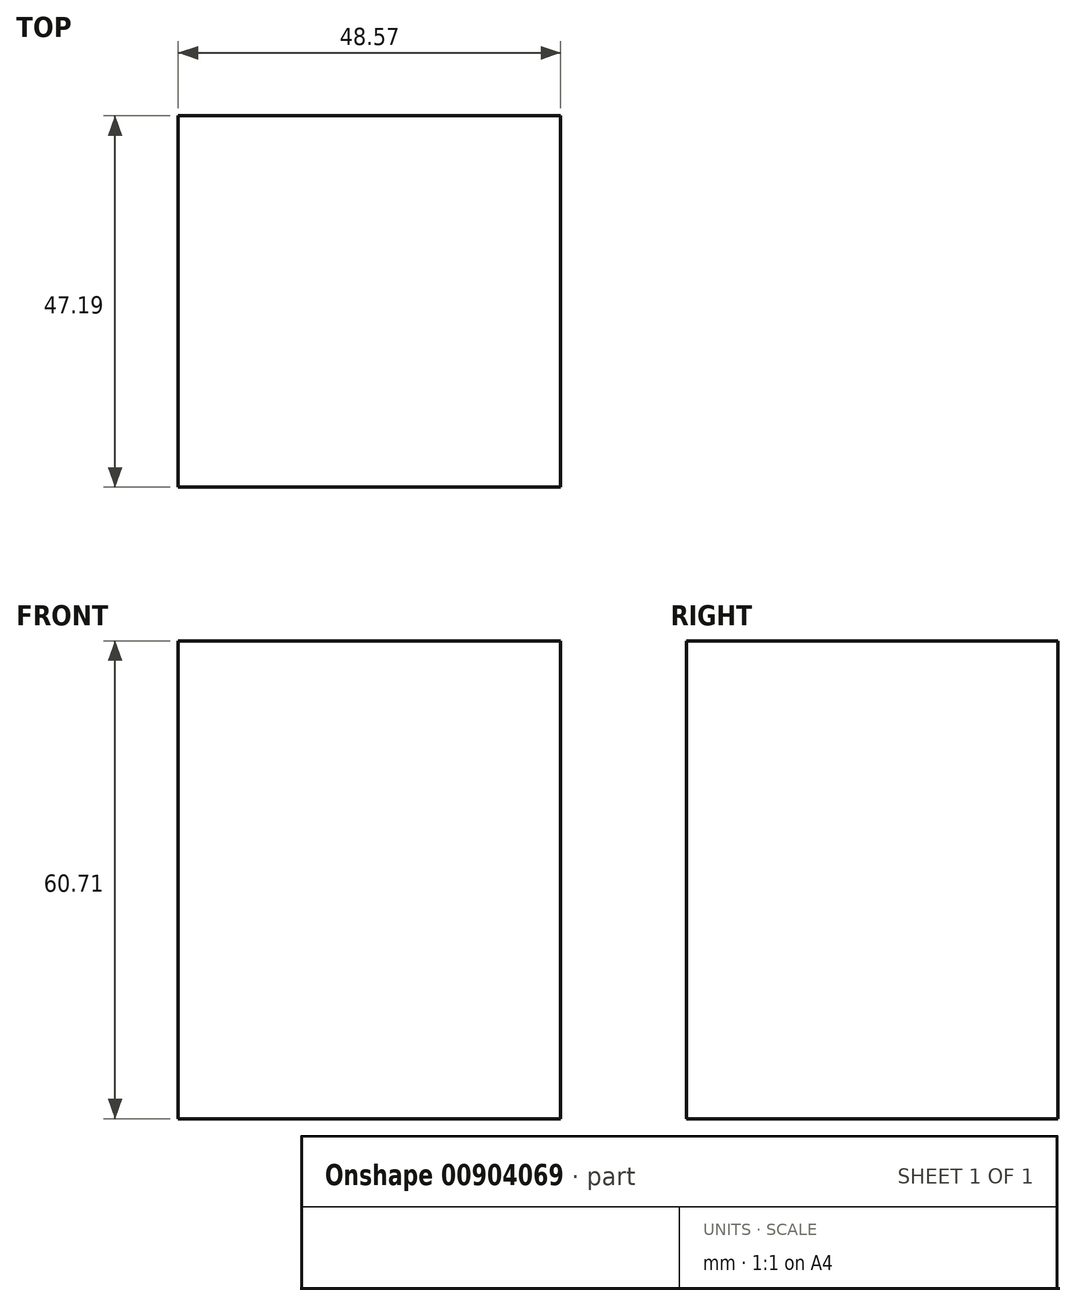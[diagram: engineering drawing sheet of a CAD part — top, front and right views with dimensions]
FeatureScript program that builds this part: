
annotation { "Feature Type Name" : "Feature", "Feature Type Description" : "" }
export const myFeature = defineFeature(function(context is Context, id is Id, definition is map)
    precondition{}
    {
        {
            var Q0;
            Q0=qCreatedBy(makeId("Top.planeOp"),FACE);
            var sketch = newSketch(context, id + "F0", { "sketchPlane" : qUnion([Q0])});
            skLineSegment(sketch, "E0.bottom", {"start": v(0, 0) * mm, "end": v(48.57, 0) * mm});
            skLineSegment(sketch, "E0.top", {"start": v(0, -47.19) * mm, "end": v(48.57, -47.19) * mm});
            skLineSegment(sketch, "E0.left", {"start": v(0, 0) * mm, "end": v(0, -47.19) * mm});
            skLineSegment(sketch, "E0.right", {"start": v(48.57, 0) * mm, "end": v(48.57, -47.19) * mm});
            skSolve(sketch);
        }
        {
            var Q0;
            Q0 = qSketchRegion(id + "F0", true);
            extrude(context, id + "F1", {"entities" : qUnion([Q0]), "depth" : 60.7 * mm, "offsetDistance" : 25.4 * mm});
        }
    });
